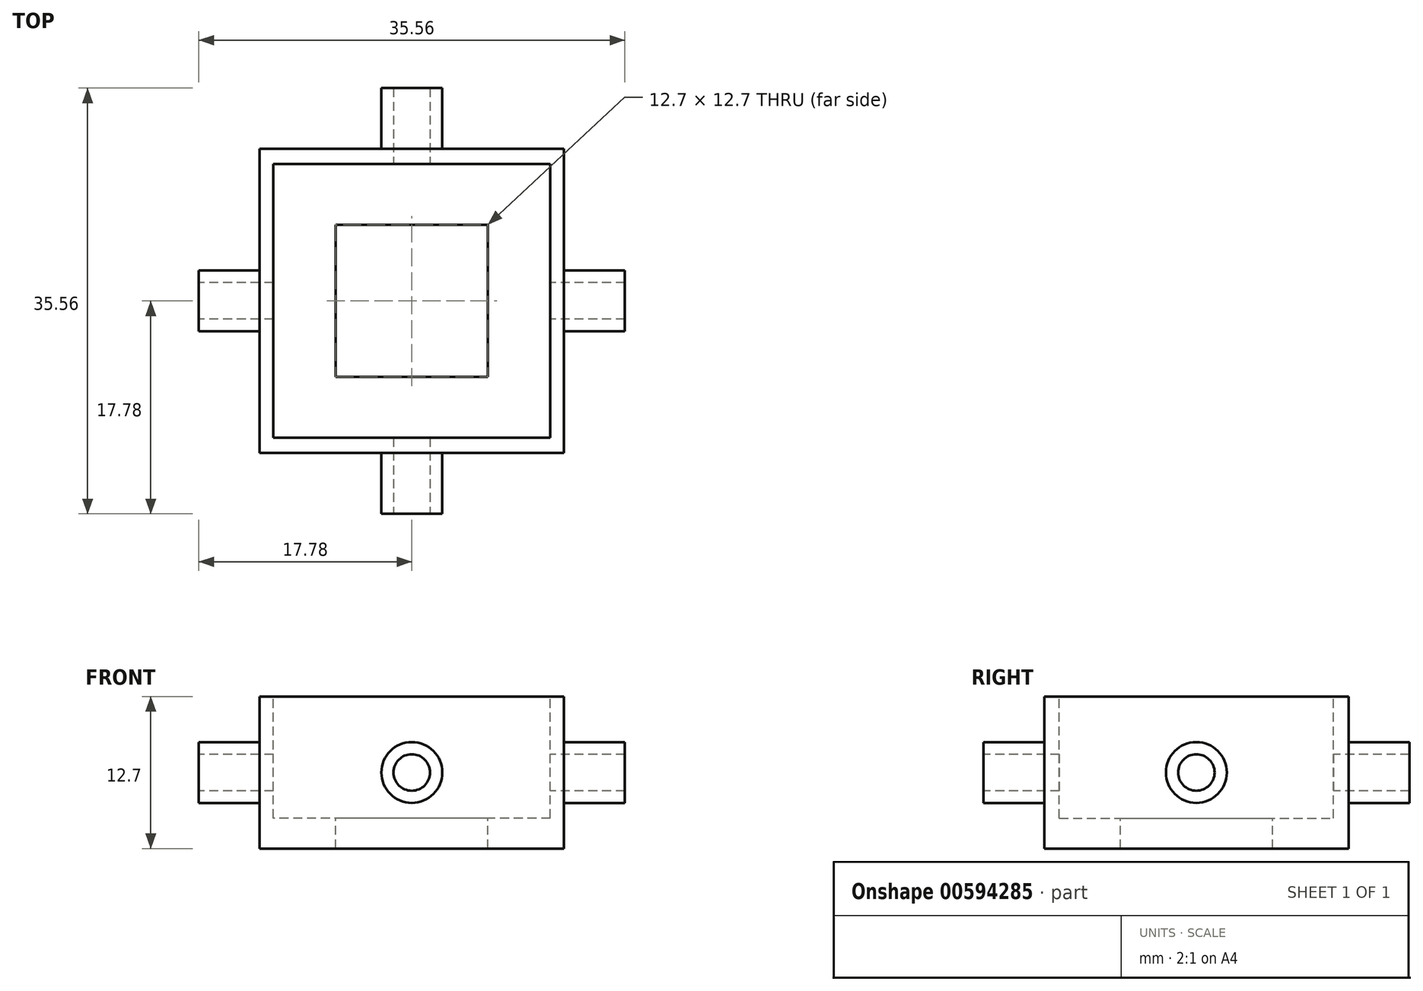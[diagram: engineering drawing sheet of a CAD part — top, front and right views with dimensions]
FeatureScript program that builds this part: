
annotation { "Feature Type Name" : "Feature", "Feature Type Description" : "" }
export const myFeature = defineFeature(function(context is Context, id is Id, definition is map)
    precondition{}
    {
        {
            var Q0;
            Q0=qCreatedBy(makeId("Top.planeOp"),FACE);
            var sketch = newSketch(context, id + "F0", { "sketchPlane" : qUnion([Q0])});
            skLineSegment(sketch, "E0.bottom", {"start": v(12.7, -12.7) * mm, "end": v(-12.7, -12.7) * mm});
            skLineSegment(sketch, "E0.top", {"start": v(12.7, 12.7) * mm, "end": v(-12.7, 12.7) * mm});
            skLineSegment(sketch, "E0.left", {"start": v(12.7, -12.7) * mm, "end": v(12.7, 12.7) * mm});
            skLineSegment(sketch, "E0.right", {"start": v(-12.7, -12.7) * mm, "end": v(-12.7, 12.7) * mm});
            skPoint(sketch, "E0.middle", {"position": v(0, 0) * mm});
            skSolve(sketch);
        }
        {
            var Q0;
            Q0 = qSketchRegion(id + "F0", true);
            extrude(context, id + "F1", {"entities" : qUnion([Q0]), "depth" : 12.7 * mm, "offsetDistance" : 25.4 * mm});
        }
        {
            var Q0;
            Q0=makeQuery(id+"F1.opExtrude","CAP_FACE",FACE,{"disambiguationData":[OSD([sQuery(id+"F0.wireOp",EDGE,"E0.bottom"),sQuery(id+"F0.wireOp",EDGE,"E0.top"),sQuery(id+"F0.wireOp",EDGE,"E0.left"),sQuery(id+"F0.wireOp",EDGE,"E0.right")])],"isStart":false});
            var sketch = newSketch(context, id + "F2", { "sketchPlane" : qUnion([Q0])});
            skLineSegment(sketch, "E1.bottom", {"start": v(11.56, -11.44) * mm, "end": v(-11.56, -11.44) * mm});
            skLineSegment(sketch, "E1.top", {"start": v(11.56, 11.44) * mm, "end": v(-11.56, 11.44) * mm});
            skLineSegment(sketch, "E1.left", {"start": v(11.56, -11.44) * mm, "end": v(11.56, 11.44) * mm});
            skLineSegment(sketch, "E1.right", {"start": v(-11.56, -11.44) * mm, "end": v(-11.56, 11.44) * mm});
            skPoint(sketch, "E1.middle", {"position": v(0, 0) * mm});
            skSolve(sketch);
        }
        {
            var Q0;
            Q0=makeQuery(id+"F2.imprint","IMPRINT",FACE,{"disambiguationData":[TD([[makeQuery(id+"F2.imprint","IMPRINT",EDGE,{"derivedFrom":sQuery(id+"F2.wireOp",EDGE,"E1.bottom")}),-1.0]])]});
            extrude(context, id + "F3", {"entities" : qUnion([Q0]), "operationType" : NewBodyOperationType.REMOVE, "oppositeDirection" : true, "depth" : 10.16 * mm, "offsetDistance" : 25.4 * mm});
        }
        {
            var Q0;
            Q0=makeQuery(id+"F1.opExtrude","SWEPT_FACE",FACE,{"disambiguationData":[OSD([sQuery(id+"F0.wireOp",EDGE,"E0.top")])]});
            var sketch = newSketch(context, id + "F4", { "sketchPlane" : qUnion([Q0])});
            skCircle(sketch, "E2", {"center": v(0, 6.35) * mm, "radius": 2.54 * mm});
            skSolve(sketch);
        }
        {
            var Q0;
            Q0 = qSketchRegion(id + "F4", true);
            extrude(context, id + "F5", {"entities" : qUnion([Q0]), "operationType" : NewBodyOperationType.ADD, "depth" : 5.08 * mm, "offsetDistance" : 25.4 * mm});
        }
        {
            var Q0;
            Q0=makeQuery(id+"F1.opExtrude","SWEPT_FACE",FACE,{"disambiguationData":[OSD([sQuery(id+"F0.wireOp",EDGE,"E0.bottom")])]});
            var sketch = newSketch(context, id + "F6", { "sketchPlane" : qUnion([Q0])});
            skCircle(sketch, "E3", {"center": v(0, 6.35) * mm, "radius": 2.54 * mm});
            skSolve(sketch);
        }
        {
            var Q0;
            Q0 = qSketchRegion(id + "F6", true);
            extrude(context, id + "F7", {"entities" : qUnion([Q0]), "operationType" : NewBodyOperationType.ADD, "depth" : 5.08 * mm, "offsetDistance" : 25.4 * mm});
        }
        {
            var Q0;
            Q0=makeQuery(id+"F7.opExtrude","CAP_FACE",FACE,{"disambiguationData":[OSD([sQuery(id+"F6.wireOp",EDGE,"E3")])],"isStart":false});
            var sketch = newSketch(context, id + "F8", { "sketchPlane" : qUnion([Q0])});
            skCircle(sketch, "E4", {"center": v(0, 6.35) * mm, "radius": 1.52 * mm});
            skSolve(sketch);
        }
        {
            var Q0;
            Q0=makeQuery(id+"F8.imprint","IMPRINT",FACE,{"disambiguationData":[TD([[makeQuery(id+"F8.imprint","IMPRINT",EDGE,{"derivedFrom":sQuery(id+"F8.wireOp",EDGE,"E4")}),1.0]])]});
            extrude(context, id + "F9", {"entities" : qUnion([Q0]), "operationType" : NewBodyOperationType.REMOVE, "endBound" : BoundingType.THROUGH_ALL, "oppositeDirection" : true, "depth" : 25.4 * mm, "offsetDistance" : 25.4 * mm});
        }
        {
            var Q0;
            Q0=makeQuery(id+"F1.opExtrude","SWEPT_FACE",FACE,{"disambiguationData":[OSD([sQuery(id+"F0.wireOp",EDGE,"E0.left")])]});
            var sketch = newSketch(context, id + "F10", { "sketchPlane" : qUnion([Q0])});
            skCircle(sketch, "E5", {"center": v(0, 6.35) * mm, "radius": 2.54 * mm});
            skSolve(sketch);
        }
        {
            var Q0;
            Q0 = qSketchRegion(id + "F10", true);
            extrude(context, id + "F11", {"entities" : qUnion([Q0]), "operationType" : NewBodyOperationType.ADD, "depth" : 5.08 * mm, "offsetDistance" : 25.4 * mm});
        }
        {
            var Q0;
            Q0=makeQuery(id+"F1.opExtrude","SWEPT_FACE",FACE,{"disambiguationData":[OSD([sQuery(id+"F0.wireOp",EDGE,"E0.right")])]});
            var sketch = newSketch(context, id + "F12", { "sketchPlane" : qUnion([Q0])});
            skCircle(sketch, "E6", {"center": v(0, 6.35) * mm, "radius": 2.54 * mm});
            skSolve(sketch);
        }
        {
            var Q0;
            Q0 = qSketchRegion(id + "F12", true);
            extrude(context, id + "F13", {"entities" : qUnion([Q0]), "operationType" : NewBodyOperationType.ADD, "depth" : 5.08 * mm, "offsetDistance" : 25.4 * mm});
        }
        {
            var Q0;
            Q0=makeQuery(id+"F13.opExtrude","CAP_FACE",FACE,{"disambiguationData":[OSD([sQuery(id+"F12.wireOp",EDGE,"E6")])],"isStart":false});
            var sketch = newSketch(context, id + "F14", { "sketchPlane" : qUnion([Q0])});
            skCircle(sketch, "E7", {"center": v(0, 6.35) * mm, "radius": 1.52 * mm});
            skSolve(sketch);
        }
        {
            var Q0;
            Q0 = qSketchRegion(id + "F14", true);
            extrude(context, id + "F15", {"entities" : qUnion([Q0]), "operationType" : NewBodyOperationType.REMOVE, "endBound" : BoundingType.THROUGH_ALL, "oppositeDirection" : true, "depth" : 25.4 * mm, "offsetDistance" : 25.4 * mm});
        }
        {
            var Q0;
            Q0=makeQuery(id+"F3.boolean.opBoolean","COPY",FACE,{"derivedFrom":makeQuery(id+"F3.opExtrude","CAP_FACE",FACE,{"disambiguationData":[OSD([sQuery(id+"F2.wireOp",EDGE,"E1.bottom"),sQuery(id+"F2.wireOp",EDGE,"E1.top"),sQuery(id+"F2.wireOp",EDGE,"E1.left"),sQuery(id+"F2.wireOp",EDGE,"E1.right")])],"isStart":false})});
            var sketch = newSketch(context, id + "F16", { "sketchPlane" : qUnion([Q0])});
            skLineSegment(sketch, "E8.bottom", {"start": v(6.35, -6.35) * mm, "end": v(-6.35, -6.35) * mm});
            skLineSegment(sketch, "E8.top", {"start": v(6.35, 6.35) * mm, "end": v(-6.35, 6.35) * mm});
            skLineSegment(sketch, "E8.left", {"start": v(6.35, -6.35) * mm, "end": v(6.35, 6.35) * mm});
            skLineSegment(sketch, "E8.right", {"start": v(-6.35, -6.35) * mm, "end": v(-6.35, 6.35) * mm});
            skPoint(sketch, "E8.middle", {"position": v(0, 0) * mm});
            skSolve(sketch);
        }
        {
            var Q0;
            Q0 = qSketchRegion(id + "F16", true);
            extrude(context, id + "F17", {"entities" : qUnion([Q0]), "operationType" : NewBodyOperationType.REMOVE, "endBound" : BoundingType.THROUGH_ALL, "oppositeDirection" : true, "depth" : 25.4 * mm, "offsetDistance" : 25.4 * mm});
        }
    });
